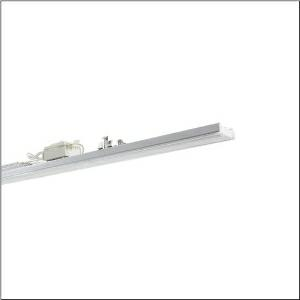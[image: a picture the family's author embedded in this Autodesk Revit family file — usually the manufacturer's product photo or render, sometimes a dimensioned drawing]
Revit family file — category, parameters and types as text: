
# Revit family: licross_r__11_recessed_mo_51tl14mn49xg_3f2a
name_source: partatom
category: Lighting Fixtures
units: mm (PartAtom-declared; Revit-internal decimal feet)

## family parameters
Cut with Voids When Loaded = No
Host = Face
Light Source = No
Part Type = Normal
Room Calculation Point = No
Round Connector Dimension = Use Diameter
Shared = No

## types (1)
- --- (1 x LED, 9470 lm, 55.2 W, 4000K)
    Apparent Load = 55 VA
    CIE Flux Codes = 56 84 97 100 100
    Color Rendering = 80
    Color Temperature = 4000K
    Default Elevation = 1800 mm
    Description = Licross® 11 Recessed MO, luminaire insert, of sheet steel, coil coated, white, length: 1.500mm, width: 66mm, height: 67mm, LED rated luminous flux: 9.470lm, light colour: 840, control gear: ON/OFF Multilumen, with plug, 3-pole, with phase selection, mains connection: 220..240V, AC, 50/60Hz, rated input power: 55W, halogen-free wiring, primary light control with lens, of plastic, primary optical cover: cover, of PMMA, light emission: direct distribution, primary light characteristic: asymmetric, protection rating (complete): IP40, insulation class (complete): insulation class I (protective earthing), certification: CE, ENEC, VDE, UKCA, protection symbol: D if used in an environment without relevant dust loads with corresponding accessories, impact resistance: IK06, permissible ambient temperature for indoor applications: -35..+40°C, corresponds to IFS (International Featured Standards) requirements for safety and quality in the food industry, reducing of maximum allowable ambient temperature of 5°C with ceiling mounting, packaging unit: 1 piece
    Height = 58 mm
    Lamp = 1 x LED
    Lamp Light Flux = 9470 lm
    Lamp Power = 55.2 W
    Lamp count = 1
    Length = 1500 mm
    Luminous efficacy = 172 lm/W
    Manufacturer = Siteco
    ModVariant = No
    Model = 51TL14MN49XG
    Mounting Place = Ceiling
    Mounting Type = Pendant
    Number of Poles = 1
    OnlyDefault = Yes
    Power Factor = 1
    Product Name = Licross® 11 Recessed MO
    Product group = luminaire insert
    ProductGroupID = 902
    Protection Class = Protection class I
    Protection Degree = IP 40
    RLX_Detail_Level = 1
    RLX_Emergency_Light_Flux = 0 lm
    RLX_Emergency_Type = 0
    RLX_Emergency_Type_DB = No
    RlxData = <blob elided: 22625 chars, md5=b68539ce>
    Socket = socket
    Standby Power = 0 W
    System Light Flux = 9470 lm
    System Power = 55 W
    Type Comments = factory setting: luminous flux: 100 % | (A | C | E) | 126 mA
    Type Image = l_1296930.jpg
    URL = http://relux.com
    VarID = @adj_085258
    Voltage = 0 V
    Weight = 0.00 kg
    Width = 66 mm

## geometry (parser evidence)
native form markers: Blend x4, Sweep x11
no freeform markers — native parametric forms only
